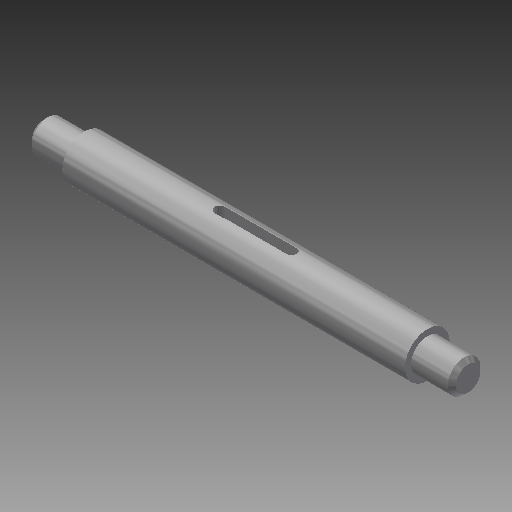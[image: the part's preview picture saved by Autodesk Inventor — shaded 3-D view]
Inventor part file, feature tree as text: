
AUTODESK INVENTOR PART (.ipt)
format: ipt  version: 2018 (Build 220112000, 112)  size: 142,336 bytes
history: native  units: mm
features: other x5, chamfer x2, revolve x1
ambient origin geometry x6: Origin, XZ Plane, XY Plane, X Axis, Y Axis, Z Axis
bodies: Solid1 (feature_tree)
feature tree (8):
  revolve  "Revolution1"  [1 undecoded]
  chamfer  "Chamfer5"  Distance=4.0mm
  other  "Keyway3"
  chamfer  "Chamfer4"  Distance=4.0mm
  other  "Start Plane"
  other  "Origin point"
  other  "Main Sketch"
  other  "iFeature3:3"
note: 1 required parameter value undecoded (feature->parameter linkage not recoverable at this tier; creation-order binding heuristic only, values carry confidence <= 0.55)
